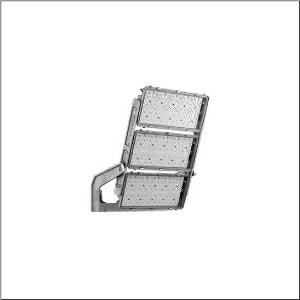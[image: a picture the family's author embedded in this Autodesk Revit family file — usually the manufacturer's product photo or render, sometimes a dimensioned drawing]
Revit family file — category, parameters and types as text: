
# Revit family: floodlight_fl_11_maxi_pro_remote___pl52_5xa779427d01aa_0793
name_source: partatom
category: Lighting Fixtures
units: mm (PartAtom-declared; Revit-internal decimal feet)

## family parameters
Cut with Voids When Loaded = No
Host = Face
Light Source = No
Part Type = Normal
Room Calculation Point = No
Round Connector Dimension = Use Diameter
Shared = No

## types (1)
- --- (1 x LED, 173640 lm, 1425.5 W, 5000K)
    Apparent Load = 1425 VA
    CIE Flux Codes = 24 55 98 100 100
    Color Rendering = 70
    Color Temperature = 5000K
    Default Elevation = 1800 mm
    Description = Floodlight FL 11  maxi  pro Remote floodlight; light control with lens of PMMA; cover panel of toughened safety glass, transparent; light distribution: PL52, asymmetric direct distribution, LEDcolour temperature: 5000K, rated luminous flux: 173.640lm, colour rendering: CRI > 70, light colour: 750; luminous efficacy: 122lm/W; brightness control: DALI 2 (1 DALI address); with terminal, 8-pole, max. 2.5mm², mains connection: 220..240V/380..400V AC, 50/60Hz, surge voltage resistance: line to ground: 10kV, ECG replaceable separately, LED unit replaceable without ESD environment, dustproof LED module, dimming range 10..100%, no afterglow with DALI off / DMX off command; 1426W floodlight with 3x LED unit of diecast aluminium, coated grey; length: 713mm / width: 651mm / height: 338mm; mounting bracket, of diecast aluminium, uncoated, natural, equipment: Power, protection rating (complete): IP66; insulation class (complete): insulation class I (protective earthing); certification: CE, ENEC, VDE; ball protection: ball impact resistance with accessories, impact resistance: IK07; rated ambient temperature 10°C, only for outdoor installations, permissible operating ambient temperature: -40..+30°C, permissible storage temperature: -40..+85°Cpackaging unit: 1 piece

Light Distribution: PL52
    Height = 320 mm
    Lamp = 1 x LED
    Lamp Light Flux = 173640 lm
    Lamp Power = 1425.5 W
    Lamp count = 1
    Length = 1002 mm
    Luminous efficacy = 122 lm/W
    Manufacturer = Siteco
    ModVariant = No
    Model = 5XA779427D01AA
    Mounting Place = Ceiling
    Mounting Type = Surface mounted
    Number of Poles = 1
    OnlyDefault = Yes
    Power Factor = 1
    Product Name = Floodlight FL 11 maxi pro Remote | PL52
    Product group = floodlight | ceiling mounted
    ProductGroupID = 301
    Protection Class = Protection class I
    Protection Degree = IP 66
    RLX_Detail_Level = 1
    RLX_Emergency_Light_Flux = 0 lm
    RLX_Emergency_Type = 0
    RLX_Emergency_Type_DB = No
    RlxData = <blob elided: 52493 chars, md5=7c720812>
    Socket = socket
    Standby Power = 0 W
    System Light Flux = 173640 lm
    System Power = 1425 W
    Type Comments = factory setting: luminous flux: 100 % | dim-lin: 254 | 980 mA
    Type Image = l_1349141.jpg
    URL = http://relux.com
    VarID = @adj_097986
    Voltage = 0 V
    Weight = 0.00 kg
    Width = 655 mm

## geometry (parser evidence)
native form markers: Blend x4, Sweep x12
no freeform markers — native parametric forms only
